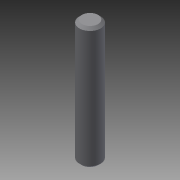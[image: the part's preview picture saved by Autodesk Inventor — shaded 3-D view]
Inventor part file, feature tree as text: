
AUTODESK INVENTOR PART (.ipt)
format: ipt  version: 2014 SP2 (Build 180246200, 246)  size: 134,144 bytes
history: native  units: in
note: dims shown in document units (in); Inventor stores cm internally (conversion verified against a paired STEP export)
features: other x112, revolve x1, sketch x1
ambient origin geometry x8: Origin, YZ Plane, XZ Plane, XY Plane, X Axis, Y Axis, Z Axis, Center Point
bodies: Solid1 (feature_tree)
feature tree (114):
  revolve  "Revolution1"  [1 undecoded]
  other  "b11_XY"
  other  "b11_YZ"
  other  "b11_ZX"
  other  "b11_X"
  other  "b11_Y"
  other  "b11_Z"
  other  "b11_Center"
  other  "b2_XY"
  other  "b2_YZ"
  other  "b2_ZX"
  other  "b2_X"
  other  "b2_Y"
  other  "b2_Z"
  other  "b2_Center"
  other  "f1_XY"
  other  "f1_YZ"
  other  "f1_ZX"
  other  "f1_X"
  other  "f1_Y"
  other  "f1_Z"
  other  "f1_Center"
  other  "f2_XY"
  other  "f2_YZ"
  other  "f2_ZX"
  other  "f2_X"
  other  "f2_Y"
  other  "f2_Z"
  other  "f2_Center"
  other  "h1_XY"
  other  "h1_YZ"
  other  "h1_ZX"
  other  "h1_X"
  other  "h1_Y"
  other  "h1_Z"
  other  "h1_Center"
  other  "h2_XY"
  other  "h2_YZ"
  other  "h2_ZX"
  other  "h2_X"
  other  "h2_Y"
  other  "h2_Z"
  other  "h2_Center"
  other  "npt1_XY"
  other  "npt1_YZ"
  other  "npt1_ZX"
  other  "npt1_X"
  other  "npt1_Y"
  other  "npt1_Z"
  other  "npt1_Center"
  other  "npt1_1_XY"
  other  "npt1_1_YZ"
  other  "npt1_1_ZX"
  other  "npt1_1_X"
  other  "npt1_1_Y"
  other  "npt1_1_Z"
  other  "npt1_1_Center"
  other  "npt2_XY"
  other  "npt2_YZ"
  other  "npt2_ZX"
  other  "npt2_X"
  other  "npt2_Y"
  other  "npt2_Z"
  other  "npt2_Center"
  other  "npt2_1_XY"
  other  "npt2_1_YZ"
  other  "npt2_1_ZX"
  other  "npt2_1_X"
  other  "npt2_1_Y"
  other  "npt2_1_Z"
  other  "npt2_1_Center"
  other  "rod_XY"
  other  "rod_YZ"
  other  "rod_ZX"
  other  "rod_X"
  other  "rod_Y"
  other  "rod_Z"
  other  "rod_Center"
  other  "rod_to_part_XY"
  other  "rod_to_part_YZ"
  other  "rod_to_part_ZX"
  other  "rod_to_part_X"
  other  "rod_to_part_Y"
  other  "rod_to_part_Z"
  other  "rod_to_part_Center"
  other  "th1_XY"
  other  "th1_YZ"
  other  "th1_ZX"
  other  "th1_X"
  other  "th1_Y"
  other  "th1_Z"
  other  "th1_Center"
  other  "th2_XY"
  other  "th2_YZ"
  other  "th2_ZX"
  other  "th2_X"
  other  "th2_Y"
  other  "th2_Z"
  other  "th2_Center"
  other  "to_rod_pivot_XY"
  other  "to_rod_pivot_YZ"
  other  "to_rod_pivot_ZX"
  other  "to_rod_pivot_X"
  other  "to_rod_pivot_Y"
  other  "to_rod_pivot_Z"
  other  "to_rod_pivot_Center"
  other  "to_rod_pivot1_XY"
  other  "to_rod_pivot1_YZ"
  other  "to_rod_pivot1_ZX"
  other  "to_rod_pivot1_X"
  other  "to_rod_pivot1_Y"
  other  "to_rod_pivot1_Z"
  other  "to_rod_pivot1_Center"
  sketch  "Sketch_10"  dims[d0=360.0deg d1=0.0in d2=0.0in d3=0.0in d4=0.0in d5=0.0in d6=0.0in d7=0.0in d8=0.0in d9=0.0in d10=0.0in d11=0.0in d12=0.0in]
note: 1 required parameter value undecoded (feature->parameter linkage not recoverable at this tier; creation-order binding heuristic only, values carry confidence <= 0.55)
